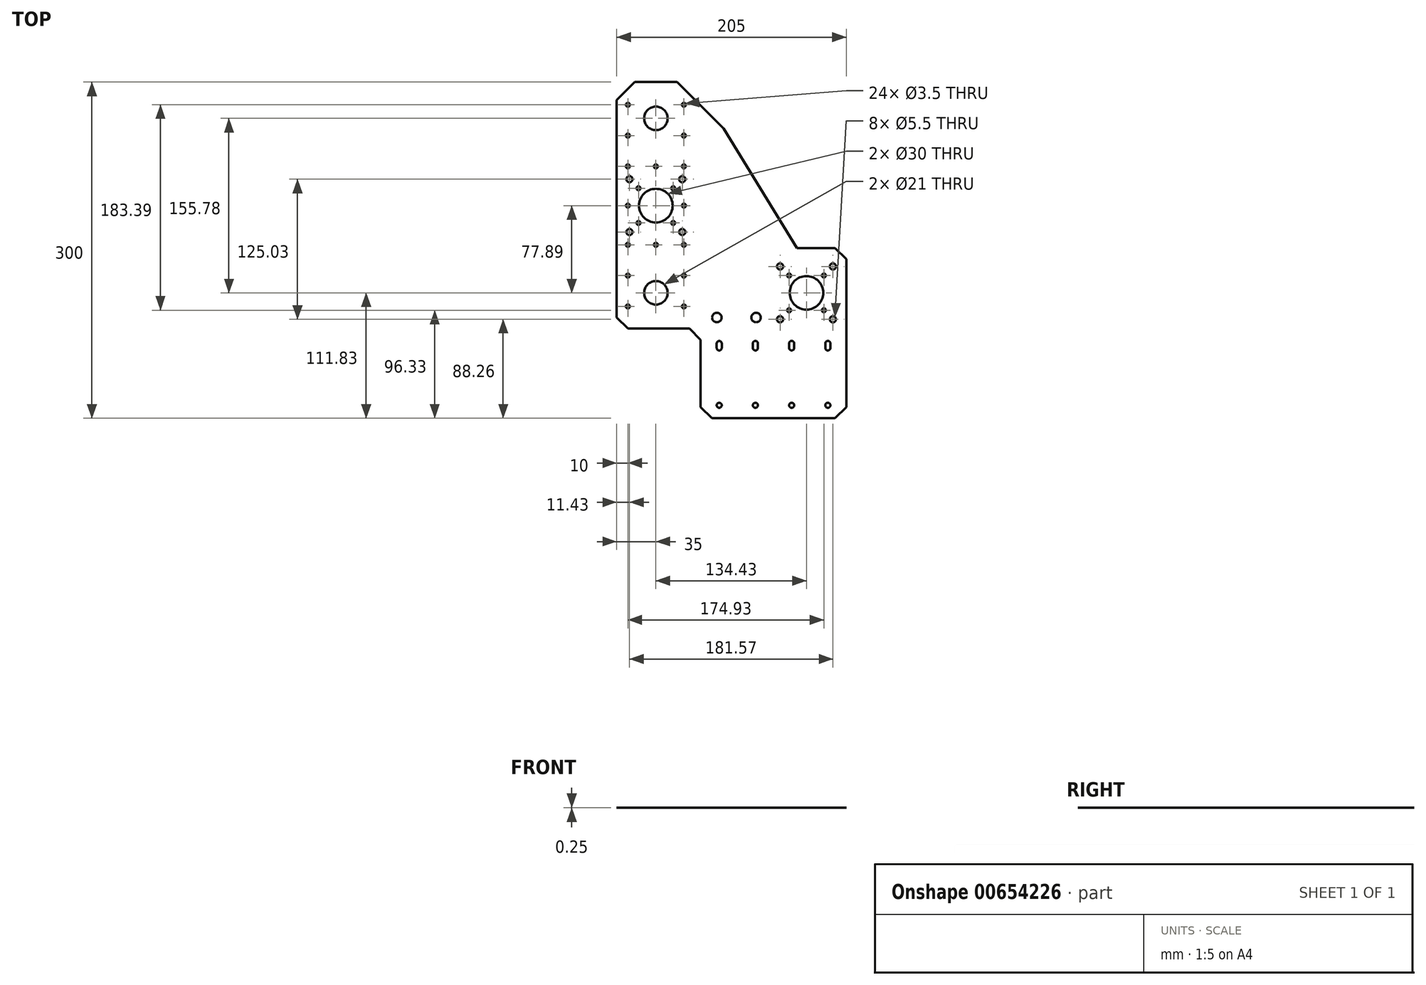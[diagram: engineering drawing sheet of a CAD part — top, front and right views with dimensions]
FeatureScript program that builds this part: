
annotation { "Feature Type Name" : "Feature", "Feature Type Description" : "" }
export const myFeature = defineFeature(function(context is Context, id is Id, definition is map)
    precondition{}
    {
        {
            var Q0;
            Q0=qCreatedBy(makeId("Top.planeOp"),FACE);
            var sketch = newSketch(context, id + "F0", { "sketchPlane" : qUnion([Q0])});
            skLineSegment(sketch, "E0", {"start": v(92.5, -150) * mm, "end": v(102.5, -140) * mm});
            skLineSegment(sketch, "E1", {"start": v(92.5, -150) * mm, "end": v(-17.5, -150) * mm});
            skLineSegment(sketch, "E2", {"start": v(-27.5, -140) * mm, "end": v(-17.5, -150) * mm});
            skLineSegment(sketch, "E3", {"start": v(-27.5, -140) * mm, "end": v(-27.5, -80) * mm});
            skLineSegment(sketch, "E4", {"start": v(-37.5, -70) * mm, "end": v(-27.5, -80) * mm});
            skLineSegment(sketch, "E5", {"start": v(-37.5, -70) * mm, "end": v(-92.5, -70) * mm});
            skLineSegment(sketch, "E6", {"start": v(-102.5, -60) * mm, "end": v(-92.5, -70) * mm});
            skLineSegment(sketch, "E7", {"start": v(-102.5, -60) * mm, "end": v(-102.5, 134) * mm});
            skLineSegment(sketch, "E8", {"start": v(-86.5, 150) * mm, "end": v(-102.5, 134) * mm});
            skLineSegment(sketch, "E9", {"start": v(-86.5, 150) * mm, "end": v(-48.5, 150) * mm});
            skLineSegment(sketch, "E10", {"start": v(-7.09, 108.59) * mm, "end": v(-48.5, 150) * mm});
            skLineSegment(sketch, "E11", {"start": v(-7.09, 108.59) * mm, "end": v(58.42, 1.83) * mm});
            skLineSegment(sketch, "E12", {"start": v(92.5, 1.83) * mm, "end": v(58.42, 1.83) * mm});
            skLineSegment(sketch, "E13", {"start": v(102.5, -8.17) * mm, "end": v(92.5, 1.83) * mm});
            skLineSegment(sketch, "E14", {"start": v(102.5, -8.17) * mm, "end": v(102.5, -140) * mm});
            skLineSegment(sketch, "E15", {"start": v(-13.2, -83.3) * mm, "end": v(-13.2, -87.3) * mm});
            skLineSegment(sketch, "E16", {"start": v(-8.7, -87.3) * mm, "end": v(-8.7, -83.3) * mm});
            skLineSegment(sketch, "E17", {"start": v(19.11, -83.3) * mm, "end": v(19.11, -87.3) * mm});
            skLineSegment(sketch, "E18", {"start": v(23.61, -87.3) * mm, "end": v(23.61, -83.3) * mm});
            skLineSegment(sketch, "E19", {"start": v(51.43, -83.3) * mm, "end": v(51.43, -87.3) * mm});
            skLineSegment(sketch, "E20", {"start": v(55.93, -87.3) * mm, "end": v(55.93, -83.3) * mm});
            skLineSegment(sketch, "E21", {"start": v(83.75, -83.3) * mm, "end": v(83.75, -87.3) * mm});
            skLineSegment(sketch, "E22", {"start": v(88.25, -87.3) * mm, "end": v(88.25, -83.3) * mm});
            skCircle(sketch, "E23", {"center": v(-42.5, 129.72) * mm, "radius": 1.75 * mm});
            skCircle(sketch, "E24", {"center": v(-92.5, 129.72) * mm, "radius": 1.75 * mm});
            skCircle(sketch, "E25", {"center": v(-92.5, 74.72) * mm, "radius": 1.75 * mm});
            skCircle(sketch, "E26", {"center": v(-92.5, 4.72) * mm, "radius": 1.75 * mm});
            skCircle(sketch, "E27", {"center": v(-92.5, -50.28) * mm, "radius": 1.75 * mm});
            skCircle(sketch, "E28", {"center": v(-42.5, -50.28) * mm, "radius": 1.75 * mm});
            skCircle(sketch, "E29", {"center": v(-42.5, 4.72) * mm, "radius": 1.75 * mm});
            skCircle(sketch, "E30", {"center": v(-42.5, 74.72) * mm, "radius": 1.75 * mm});
            skCircle(sketch, "E31", {"center": v(-92.5, 102.22) * mm, "radius": 1.75 * mm});
            skCircle(sketch, "E32", {"center": v(-42.5, 102.22) * mm, "radius": 1.75 * mm});
            skCircle(sketch, "E33", {"center": v(-67.5, 74.72) * mm, "radius": 1.75 * mm});
            skCircle(sketch, "E34", {"center": v(-92.5, 39.72) * mm, "radius": 1.75 * mm});
            skCircle(sketch, "E35", {"center": v(-42.5, 39.72) * mm, "radius": 1.75 * mm});
            skCircle(sketch, "E36", {"center": v(-92.5, -22.78) * mm, "radius": 1.75 * mm});
            skCircle(sketch, "E37", {"center": v(-42.5, -22.78) * mm, "radius": 1.75 * mm});
            skCircle(sketch, "E38", {"center": v(-67.5, 4.72) * mm, "radius": 1.75 * mm});
            skCircle(sketch, "E39", {"center": v(-10.96, -138.5) * mm, "radius": 2.25 * mm});
            skCircle(sketch, "E40", {"center": v(21.36, -138.5) * mm, "radius": 2.25 * mm});
            skCircle(sketch, "E41", {"center": v(53.68, -138.5) * mm, "radius": 2.25 * mm});
            skCircle(sketch, "E42", {"center": v(86, -138.5) * mm, "radius": 2.25 * mm});
            skCircle(sketch, "E43", {"center": v(-52, 55.22) * mm, "radius": 1.75 * mm});
            skCircle(sketch, "E44", {"center": v(-52, 24.22) * mm, "radius": 1.75 * mm});
            skCircle(sketch, "E45", {"center": v(-67.5, 39.72) * mm, "radius": 15 * mm});
            skCircle(sketch, "E46", {"center": v(-83, 24.22) * mm, "radius": 1.75 * mm});
            skCircle(sketch, "E47", {"center": v(-83, 55.22) * mm, "radius": 1.75 * mm});
            skCircle(sketch, "E48", {"center": v(-91.07, 63.3) * mm, "radius": 2.75 * mm});
            skCircle(sketch, "E49", {"center": v(-43.93, 63.3) * mm, "radius": 2.75 * mm});
            skCircle(sketch, "E50", {"center": v(-43.93, 16.15) * mm, "radius": 2.75 * mm});
            skCircle(sketch, "E51", {"center": v(-91.07, 16.15) * mm, "radius": 2.75 * mm});
            skCircle(sketch, "E52", {"center": v(-67.5, -38.17) * mm, "radius": 10.5 * mm});
            skCircle(sketch, "E53", {"center": v(-67.5, 117.61) * mm, "radius": 10.5 * mm});
            skCircle(sketch, "E54", {"center": v(-13.07, -60.17) * mm, "radius": 4.25 * mm});
            skCircle(sketch, "E55", {"center": v(21.93, -60.17) * mm, "radius": 4.25 * mm});
            skCircle(sketch, "E56", {"center": v(43.36, -14.6) * mm, "radius": 2.75 * mm});
            skCircle(sketch, "E57", {"center": v(90.5, -14.6) * mm, "radius": 2.75 * mm});
            skCircle(sketch, "E58", {"center": v(90.5, -61.74) * mm, "radius": 2.75 * mm});
            skCircle(sketch, "E59", {"center": v(43.36, -61.74) * mm, "radius": 2.75 * mm});
            skCircle(sketch, "E60", {"center": v(66.93, -38.17) * mm, "radius": 15 * mm});
            skCircle(sketch, "E61", {"center": v(51.43, -53.67) * mm, "radius": 1.75 * mm});
            skCircle(sketch, "E62", {"center": v(82.43, -22.67) * mm, "radius": 1.75 * mm});
            skCircle(sketch, "E63", {"center": v(82.43, -53.67) * mm, "radius": 1.75 * mm});
            skCircle(sketch, "E64", {"center": v(51.43, -22.67) * mm, "radius": 1.75 * mm});
            skArc(sketch, "E65", {"start": v(-8.7, -83.3) * mm, "mid": v(-10.96, -81.05) * mm, "end": v(-13.2, -83.3) * mm});
            skArc(sketch, "E66", {"start": v(-13.2, -87.3) * mm, "mid": v(-10.96, -89.55) * mm, "end": v(-8.7, -87.3) * mm});
            skArc(sketch, "E67", {"start": v(23.61, -83.3) * mm, "mid": v(21.36, -81.05) * mm, "end": v(19.11, -83.3) * mm});
            skArc(sketch, "E68", {"start": v(19.11, -87.3) * mm, "mid": v(21.36, -89.55) * mm, "end": v(23.61, -87.3) * mm});
            skArc(sketch, "E69", {"start": v(55.93, -83.3) * mm, "mid": v(53.68, -81.05) * mm, "end": v(51.43, -83.3) * mm});
            skArc(sketch, "E70", {"start": v(51.43, -87.3) * mm, "mid": v(53.68, -89.55) * mm, "end": v(55.93, -87.3) * mm});
            skArc(sketch, "E71", {"start": v(88.25, -83.3) * mm, "mid": v(86, -81.05) * mm, "end": v(83.75, -83.3) * mm});
            skArc(sketch, "E72", {"start": v(83.75, -87.3) * mm, "mid": v(86, -89.55) * mm, "end": v(88.25, -87.3) * mm});
            skSolve(sketch);
        }
        {
            var Q0;
            Q0=makeQuery(id+"F0.imprint","IMPRINT",FACE,{"disambiguationData":[TD([[makeQuery(id+"F0.imprint","IMPRINT",EDGE,{"derivedFrom":sQuery(id+"F0.wireOp",EDGE,"E0")}),1.0]])]});
            extrude(context, id + "F1", {"entities" : qUnion([Q0]), "depth" : 0.25 * mm, "offsetDistance" : 25.4 * mm});
        }
    });
